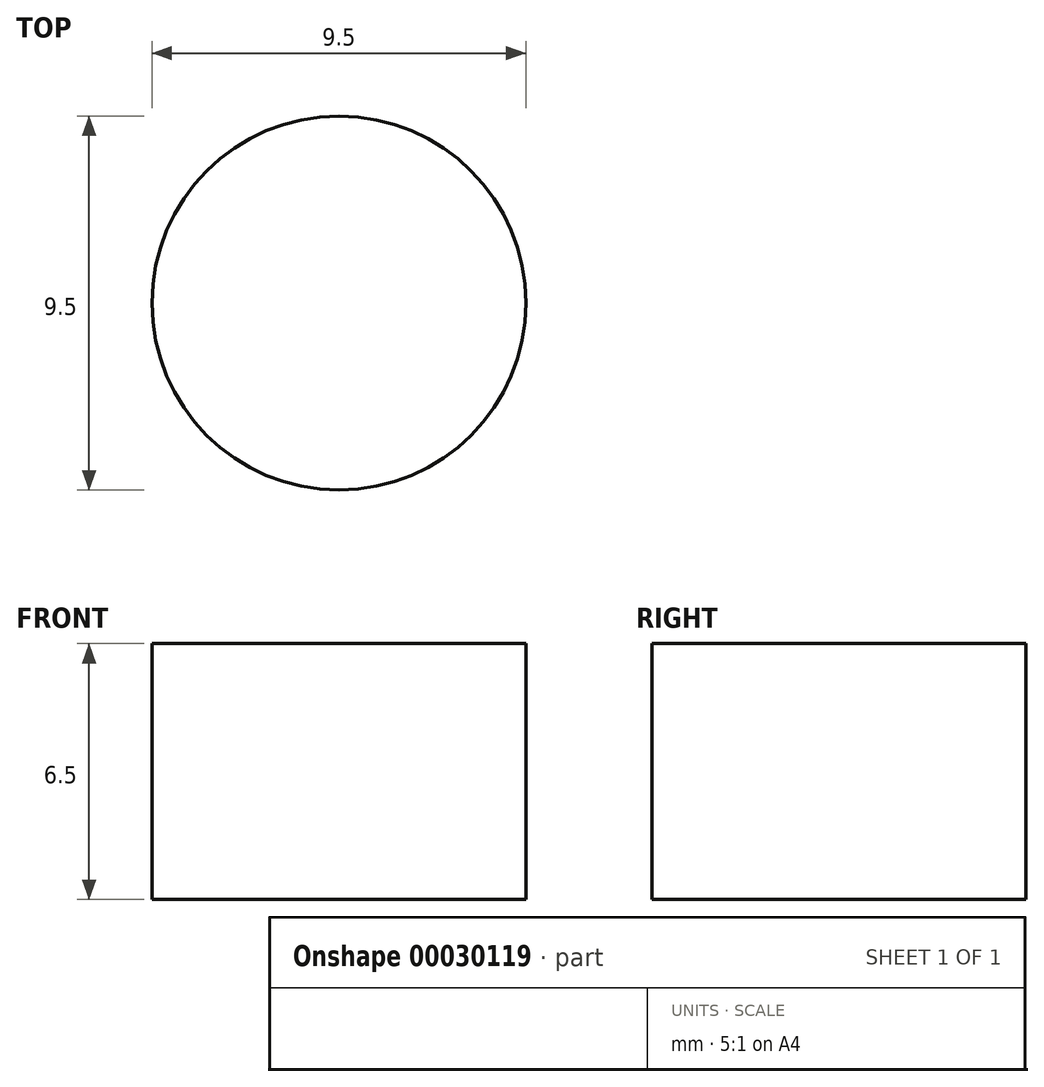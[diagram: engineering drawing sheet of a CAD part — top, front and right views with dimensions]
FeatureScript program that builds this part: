
annotation { "Feature Type Name" : "Feature", "Feature Type Description" : "" }
export const myFeature = defineFeature(function(context is Context, id is Id, definition is map)
    precondition{}
    {
        {
            var Q0;
            Q0=qCreatedBy(makeId("Top.planeOp"),FACE);
            var sketch = newSketch(context, id + "F0", { "sketchPlane" : qUnion([Q0])});
            skCircle(sketch, "E0", {"center": v(0, 0) * mm, "radius": 4.75 * mm});
            skSolve(sketch);
        }
        {
            var Q0;
            Q0=makeQuery(id+"F0.imprint","IMPRINT",FACE,{"disambiguationData":[TD([[makeQuery(id+"F0.imprint","IMPRINT",EDGE,{"derivedFrom":sQuery(id+"F0.wireOp",EDGE,"E0")}),1.0]])]});
            extrude(context, id + "F1", {"entities" : qUnion([Q0]), "depth" : 6.5 * mm});
        }
    });
